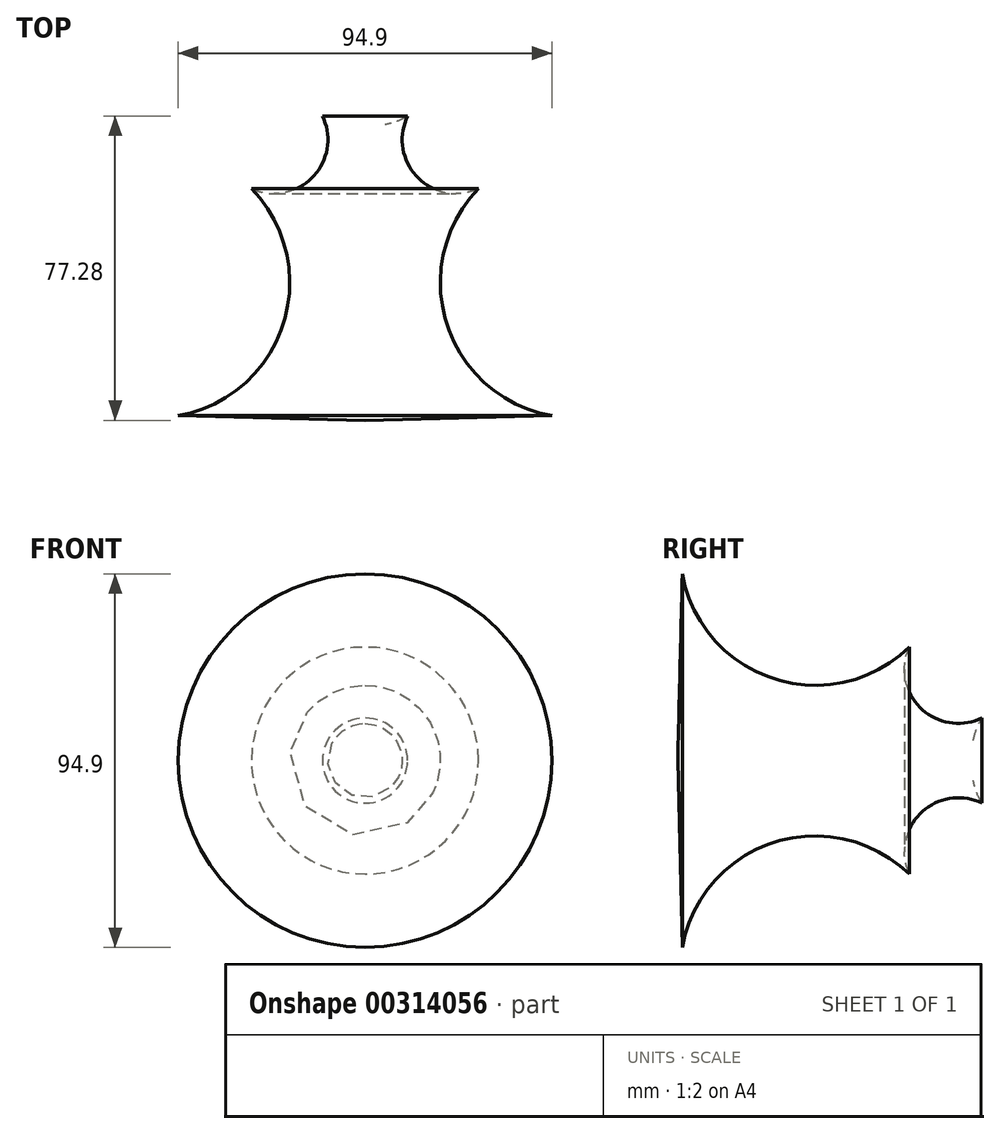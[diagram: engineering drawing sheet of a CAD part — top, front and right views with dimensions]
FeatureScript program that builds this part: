
annotation { "Feature Type Name" : "Feature", "Feature Type Description" : "" }
export const myFeature = defineFeature(function(context is Context, id is Id, definition is map)
    precondition{}
    {
        {
            var Q0;
            Q0=qCreatedBy(makeId("Top.planeOp"),FACE);
            var sketch = newSketch(context, id + "F0", { "sketchPlane" : qUnion([Q0])});
            skLineSegment(sketch, "E0", {"start": v(0, 56.52) * mm, "end": v(0, -49.54) * mm});
            skArc(sketch, "E1", {"start": v(0, 25.58) * mm, "mid": v(18.21, 41.05) * mm, "end": v(0, 56.52) * mm});
            skArc(sketch, "E2", {"start": v(10.81, 27.74) * mm, "mid": v(13.35, 12.19) * mm, "end": v(28.84, 9.3) * mm});
            skArc(sketch, "E3", {"start": v(28.84, 9.3) * mm, "mid": v(20.78, -25.14) * mm, "end": v(47.45, -48.38) * mm});
            skLineSegment(sketch, "E4", {"start": v(0, -49.54) * mm, "end": v(47.45, -48.38) * mm});
            skSolve(sketch);
        }
        {
            var Q0;
            Q0 = qSketchRegion(id + "F0", true);
            var Q1;
            Q1=sQuery(id+"F0.wireOp",EDGE,"E0");
            revolve(context, id + "F1", {"entities" : qUnion([Q0]), "axis" : qUnion([Q1]), "revolveType" : RevolveType.FULL});
        }
    });
